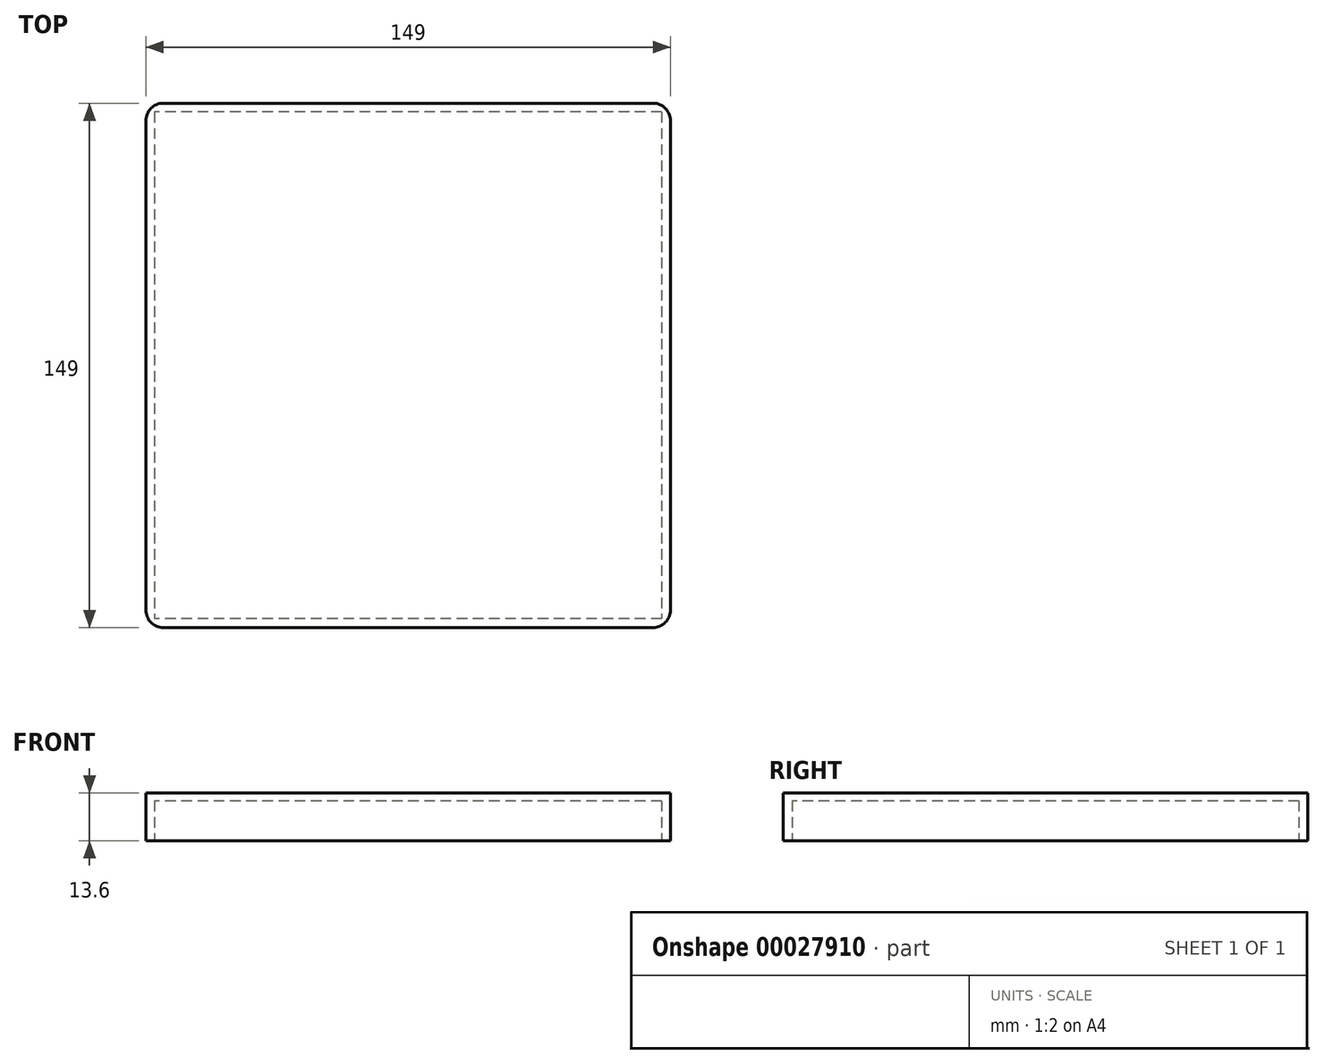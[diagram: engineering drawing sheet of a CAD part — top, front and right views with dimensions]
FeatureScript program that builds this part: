
annotation { "Feature Type Name" : "Feature", "Feature Type Description" : "" }
export const myFeature = defineFeature(function(context is Context, id is Id, definition is map)
    precondition{}
    {
        {
            var Q0;
            Q0=qCreatedBy(makeId("Top.planeOp"),FACE);
            var sketch = newSketch(context, id + "F0", { "sketchPlane" : qUnion([Q0])});
            skLineSegment(sketch, "E0.rect.bottom", {"start": v(72, 72) * mm, "end": v(-72, 72) * mm});
            skLineSegment(sketch, "E0.rect.top", {"start": v(72, -72) * mm, "end": v(-72, -72) * mm});
            skLineSegment(sketch, "E0.rect.left", {"start": v(72, 72) * mm, "end": v(72, -72) * mm});
            skLineSegment(sketch, "E0.rect.right", {"start": v(-72, 72) * mm, "end": v(-72, -72) * mm});
            skPoint(sketch, "E0.rect.middle", {"position": v(0, 0) * mm});
            skLineSegment(sketch, "E1.rect.bottom", {"start": v(74.5, -74.5) * mm, "end": v(-74.5, -74.5) * mm});
            skLineSegment(sketch, "E1.rect.top", {"start": v(74.5, 74.5) * mm, "end": v(-74.5, 74.5) * mm});
            skLineSegment(sketch, "E1.rect.left", {"start": v(74.5, -74.5) * mm, "end": v(74.5, 74.5) * mm});
            skLineSegment(sketch, "E1.rect.right", {"start": v(-74.5, -74.5) * mm, "end": v(-74.5, 74.5) * mm});
            skSolve(sketch);
        }
        {
            var Q0;
            Q0 = qSketchRegion(id + "F0", true);
            extrude(context, id + "F1", {"entities" : qUnion([Q0]), "depth" : 11.35 * mm});
        }
        {
            var Q0;
            Q0=makeQuery(id+"F1.opExtrude","CAP_FACE",FACE,{"disambiguationData":[OSD([sQuery(id+"F0.wireOp",EDGE,"E0.rect.bottom"),sQuery(id+"F0.wireOp",EDGE,"E0.rect.top"),sQuery(id+"F0.wireOp",EDGE,"E0.rect.left"),sQuery(id+"F0.wireOp",EDGE,"E0.rect.right"),sQuery(id+"F0.wireOp",EDGE,"E1.rect.bottom"),sQuery(id+"F0.wireOp",EDGE,"E1.rect.top"),sQuery(id+"F0.wireOp",EDGE,"E1.rect.left"),sQuery(id+"F0.wireOp",EDGE,"E1.rect.right")])],"isStart":false});
            var sketch = newSketch(context, id + "F2", { "sketchPlane" : qUnion([Q0])});
            skLineSegment(sketch, "E2.bottom", {"start": v(74.5, 74.5) * mm, "end": v(-74.5, 74.5) * mm});
            skLineSegment(sketch, "E2.top", {"start": v(74.5, -74.5) * mm, "end": v(-74.5, -74.5) * mm});
            skLineSegment(sketch, "E2.left", {"start": v(74.5, 74.5) * mm, "end": v(74.5, -74.5) * mm});
            skLineSegment(sketch, "E2.right", {"start": v(-74.5, 74.5) * mm, "end": v(-74.5, -74.5) * mm});
            skSolve(sketch);
        }
        {
            var Q0;
            Q0 = qSketchRegion(id + "F2", true);
            extrude(context, id + "F3", {"entities" : qUnion([Q0]), "operationType" : NewBodyOperationType.ADD, "depth" : 2.25 * mm});
        }
        {
            var Q0;
            Q0=makeQuery(id+"F3.boolean.opBoolean","MERGE",EDGE,{"derivedFrom":[makeQuery(id+"F1.opExtrude","SWEPT_EDGE",EDGE,{"disambiguationData":[OSD([sQuery(id+"F0.wireOp",EDGE,"E1.rect.top"),sQuery(id+"F0.wireOp",EDGE,"E1.rect.left")])]}),makeQuery(id+"F3.opExtrude","SWEPT_EDGE",EDGE,{"disambiguationData":[OSD([sQuery(id+"F2.wireOp",EDGE,"E2.bottom"),sQuery(id+"F2.wireOp",EDGE,"E2.left")])]})]});
            var Q1;
            Q1=makeQuery(id+"F3.boolean.opBoolean","MERGE",EDGE,{"derivedFrom":[makeQuery(id+"F1.opExtrude","SWEPT_EDGE",EDGE,{"disambiguationData":[OSD([sQuery(id+"F0.wireOp",EDGE,"E1.rect.bottom"),sQuery(id+"F0.wireOp",EDGE,"E1.rect.left")])]}),makeQuery(id+"F3.opExtrude","SWEPT_EDGE",EDGE,{"disambiguationData":[OSD([sQuery(id+"F2.wireOp",EDGE,"E2.top"),sQuery(id+"F2.wireOp",EDGE,"E2.left")])]})]});
            var Q2;
            Q2=makeQuery(id+"F3.boolean.opBoolean","MERGE",EDGE,{"derivedFrom":[makeQuery(id+"F1.opExtrude","SWEPT_EDGE",EDGE,{"disambiguationData":[OSD([sQuery(id+"F0.wireOp",EDGE,"E1.rect.bottom"),sQuery(id+"F0.wireOp",EDGE,"E1.rect.right")])]}),makeQuery(id+"F3.opExtrude","SWEPT_EDGE",EDGE,{"disambiguationData":[OSD([sQuery(id+"F2.wireOp",EDGE,"E2.top"),sQuery(id+"F2.wireOp",EDGE,"E2.right")])]})]});
            var Q3;
            Q3=makeQuery(id+"F3.boolean.opBoolean","MERGE",EDGE,{"derivedFrom":[makeQuery(id+"F1.opExtrude","SWEPT_EDGE",EDGE,{"disambiguationData":[OSD([sQuery(id+"F0.wireOp",EDGE,"E1.rect.top"),sQuery(id+"F0.wireOp",EDGE,"E1.rect.right")])]}),makeQuery(id+"F3.opExtrude","SWEPT_EDGE",EDGE,{"disambiguationData":[OSD([sQuery(id+"F2.wireOp",EDGE,"E2.bottom"),sQuery(id+"F2.wireOp",EDGE,"E2.right")])]})]});
            fillet(context, id + "F4", {"entities" : qUnion([Q0, Q1, Q2, Q3]), "radius" : 5 * mm, "tangentPropagation" : true, "allowEdgeOverflow" : false});
        }
    });
